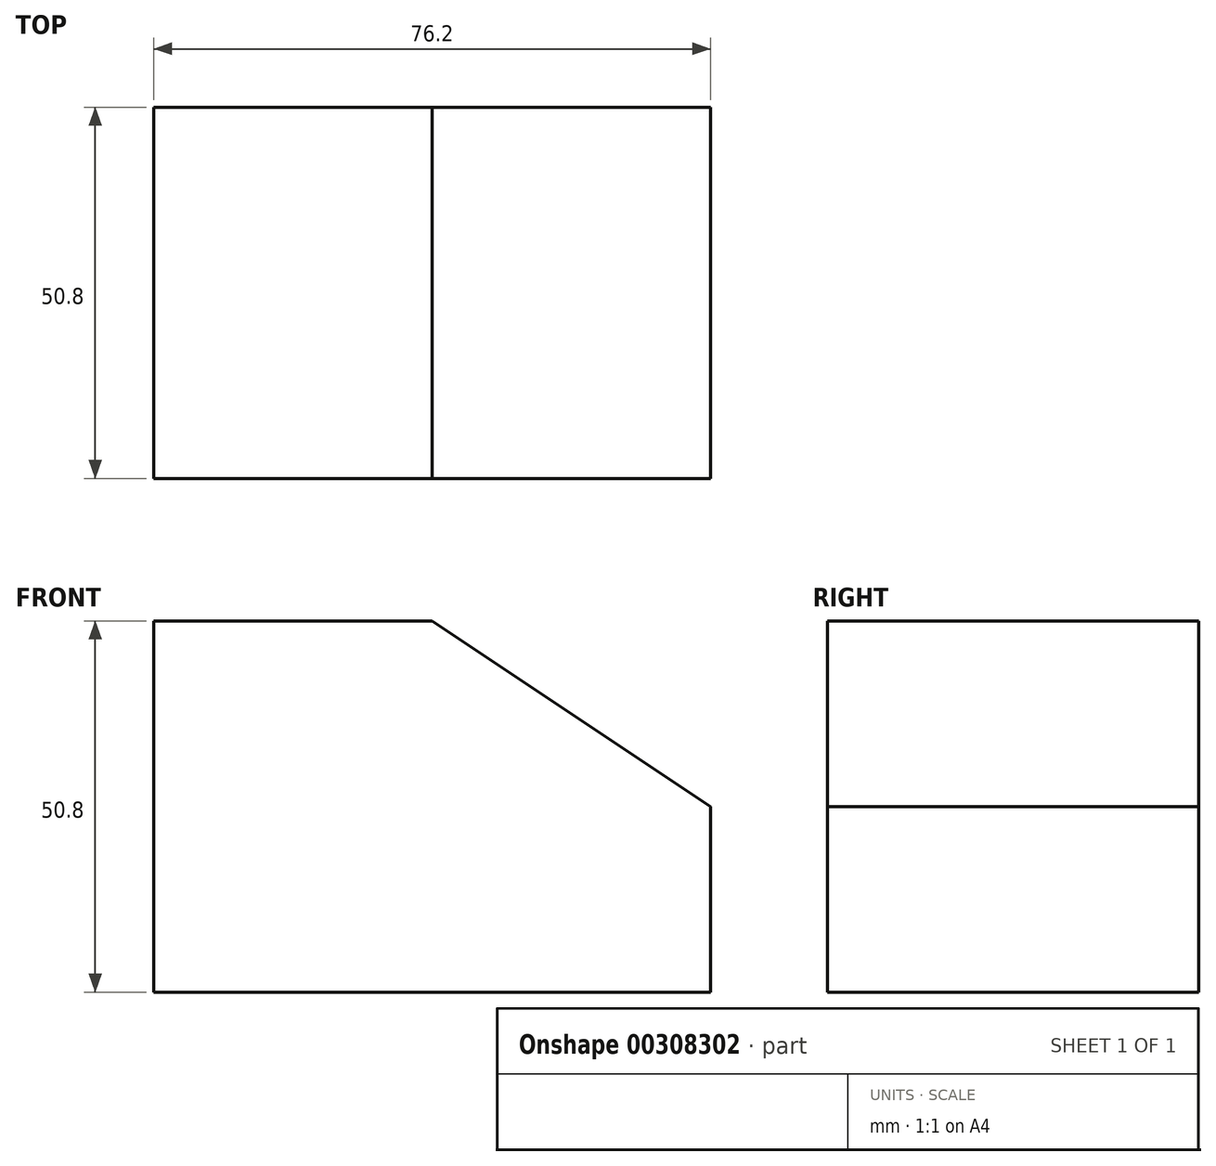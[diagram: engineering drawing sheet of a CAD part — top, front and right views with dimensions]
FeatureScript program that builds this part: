
annotation { "Feature Type Name" : "Feature", "Feature Type Description" : "" }
export const myFeature = defineFeature(function(context is Context, id is Id, definition is map)
    precondition{}
    {
        {
            var Q0;
            Q0=qCreatedBy(makeId("Front.planeOp"),FACE);
            var sketch = newSketch(context, id + "F0", { "sketchPlane" : qUnion([Q0])});
            skLineSegment(sketch, "E0", {"start": v(-43.35, -40.3) * mm, "end": v(32.85, -40.3) * mm});
            skLineSegment(sketch, "E1", {"start": v(-43.35, -40.3) * mm, "end": v(-43.35, 10.5) * mm});
            skLineSegment(sketch, "E2", {"start": v(-43.35, 10.5) * mm, "end": v(-5.25, 10.5) * mm});
            skLineSegment(sketch, "E3", {"start": v(32.85, -40.3) * mm, "end": v(32.85, -14.9) * mm});
            skLineSegment(sketch, "E4", {"start": v(32.85, -14.9) * mm, "end": v(-5.25, 10.5) * mm});
            skSolve(sketch);
        }
        {
            var Q0;
            Q0=makeQuery(id+"F0.imprint","IMPRINT",FACE,{"disambiguationData":[TD([[makeQuery(id+"F0.imprint","IMPRINT",EDGE,{"derivedFrom":sQuery(id+"F0.wireOp",EDGE,"E0")}),1.0]])]});
            extrude(context, id + "F1", {"entities" : qUnion([Q0]), "depth" : 50.8 * mm});
        }
    });
